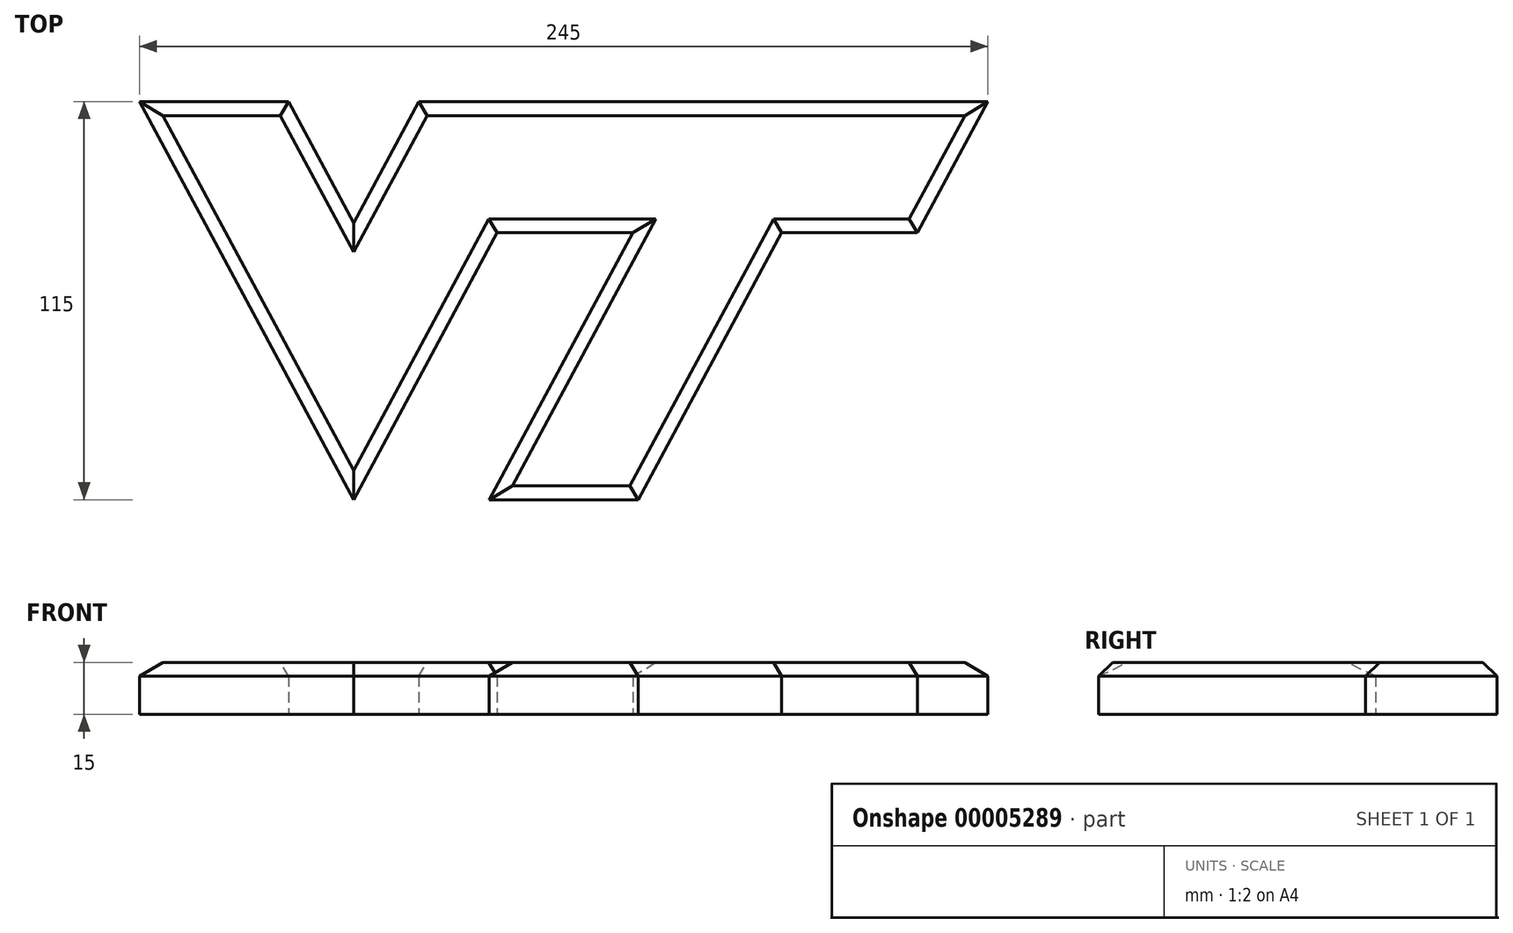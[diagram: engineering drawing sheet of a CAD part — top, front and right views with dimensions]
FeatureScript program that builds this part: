
annotation { "Feature Type Name" : "Feature", "Feature Type Description" : "" }
export const myFeature = defineFeature(function(context is Context, id is Id, definition is map)
    precondition{}
    {
        {
            var Q0;
            Q0=qCreatedBy(makeId("Top.planeOp"),FACE);
            var sketch = newSketch(context, id + "F0", { "sketchPlane" : qUnion([Q0])});
            skLineSegment(sketch, "E0", {"start": v(-123.36, 56.8) * mm, "end": v(-80.36, 56.8) * mm});
            skLineSegment(sketch, "E1", {"start": v(-20.1, 18.92) * mm, "end": v(-61.55, -58.2) * mm});
            skLineSegment(sketch, "E2", {"start": v(-61.55, -58.2) * mm, "end": v(-123.36, 56.8) * mm});
            skLineSegment(sketch, "E3", {"start": v(-80.36, 56.8) * mm, "end": v(-61.55, 21.8) * mm});
            skLineSegment(sketch, "E4", {"start": v(-61.55, 21.8) * mm, "end": v(-42.74, 56.8) * mm});
            skLineSegment(sketch, "E5", {"start": v(121.64, 56.8) * mm, "end": v(101.28, 18.92) * mm});
            skLineSegment(sketch, "E6", {"start": v(101.28, 18.92) * mm, "end": v(62.1, 18.92) * mm});
            skLineSegment(sketch, "E7", {"start": v(62.1, 18.92) * mm, "end": v(20.64, -58.2) * mm});
            skLineSegment(sketch, "E8", {"start": v(20.64, -58.2) * mm, "end": v(-22.36, -58.2) * mm});
            skLineSegment(sketch, "E9", {"start": v(-22.36, -58.2) * mm, "end": v(19.1, 18.92) * mm});
            skLineSegment(sketch, "E10", {"start": v(19.1, 18.92) * mm, "end": v(-20.1, 18.92) * mm});
            skLineSegment(sketch, "E11", {"start": v(-42.74, 56.8) * mm, "end": v(121.64, 56.8) * mm});
            skSolve(sketch);
        }
        {
            var Q0;
            Q0 = qSketchRegion(id + "F0", true);
            extrude(context, id + "F1", {"entities" : qUnion([Q0]), "depth" : 15 * mm});
        }
        {
            var Q0;
            Q0=makeQuery(id+"F1.opExtrude","CAP_EDGE",EDGE,{"disambiguationData":[OSD([sQuery(id+"F0.wireOp",EDGE,"E2")])],"isStart":false});
            var Q1;
            Q1=makeQuery(id+"F1.opExtrude","CAP_EDGE",EDGE,{"disambiguationData":[OSD([sQuery(id+"F0.wireOp",EDGE,"E1")])],"isStart":false});
            var Q2;
            Q2=makeQuery(id+"F1.opExtrude","CAP_EDGE",EDGE,{"disambiguationData":[OSD([sQuery(id+"F0.wireOp",EDGE,"E10")])],"isStart":false});
            var Q3;
            Q3=makeQuery(id+"F1.opExtrude","CAP_EDGE",EDGE,{"disambiguationData":[OSD([sQuery(id+"F0.wireOp",EDGE,"E9")])],"isStart":false});
            var Q4;
            Q4=makeQuery(id+"F1.opExtrude","CAP_EDGE",EDGE,{"disambiguationData":[OSD([sQuery(id+"F0.wireOp",EDGE,"E8")])],"isStart":false});
            var Q5;
            Q5=makeQuery(id+"F1.opExtrude","CAP_EDGE",EDGE,{"disambiguationData":[OSD([sQuery(id+"F0.wireOp",EDGE,"E7")])],"isStart":false});
            var Q6;
            Q6=makeQuery(id+"F1.opExtrude","CAP_EDGE",EDGE,{"disambiguationData":[OSD([sQuery(id+"F0.wireOp",EDGE,"E6")])],"isStart":false});
            var Q7;
            Q7=makeQuery(id+"F1.opExtrude","CAP_EDGE",EDGE,{"disambiguationData":[OSD([sQuery(id+"F0.wireOp",EDGE,"E5")])],"isStart":false});
            var Q8;
            Q8=makeQuery(id+"F1.opExtrude","CAP_EDGE",EDGE,{"disambiguationData":[OSD([sQuery(id+"F0.wireOp",EDGE,"E11")])],"isStart":false});
            var Q9;
            Q9=makeQuery(id+"F1.opExtrude","CAP_EDGE",EDGE,{"disambiguationData":[OSD([sQuery(id+"F0.wireOp",EDGE,"E4")])],"isStart":false});
            var Q10;
            Q10=makeQuery(id+"F1.opExtrude","CAP_EDGE",EDGE,{"disambiguationData":[OSD([sQuery(id+"F0.wireOp",EDGE,"E3")])],"isStart":false});
            var Q11;
            Q11=makeQuery(id+"F1.opExtrude","CAP_EDGE",EDGE,{"disambiguationData":[OSD([sQuery(id+"F0.wireOp",EDGE,"E0")])],"isStart":false});
            chamfer(context, id + "F2", {"entities" : qUnion([Q0, Q1, Q2, Q3, Q4, Q5, Q6, Q7, Q8, Q9, Q10, Q11]), "width" : 4 * mm, "tangentPropagation" : true});
        }
    });
